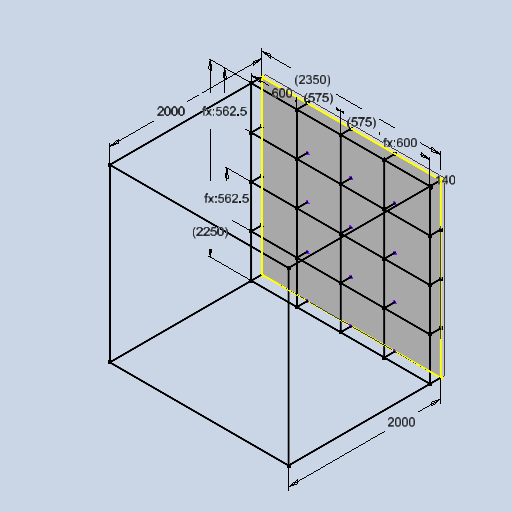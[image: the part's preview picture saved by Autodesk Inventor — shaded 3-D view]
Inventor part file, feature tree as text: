
AUTODESK INVENTOR PART (.ipt)
format: ipt  version: 2025 (Build 290162010, 162A)  size: 136,704 bytes
history: native  units: mm
features: extrude x1, sketch x1
ambient origin geometry x8: Origin, YZ Plane, XZ Plane, XY Plane, X Axis, Y Axis, Z Axis, Center Point
bodies: Solid1 (feature_tree)
feature tree (2):
  extrude  "Extrusion1"  Depth=2350.0mm
  sketch  "3D Sketch1"
